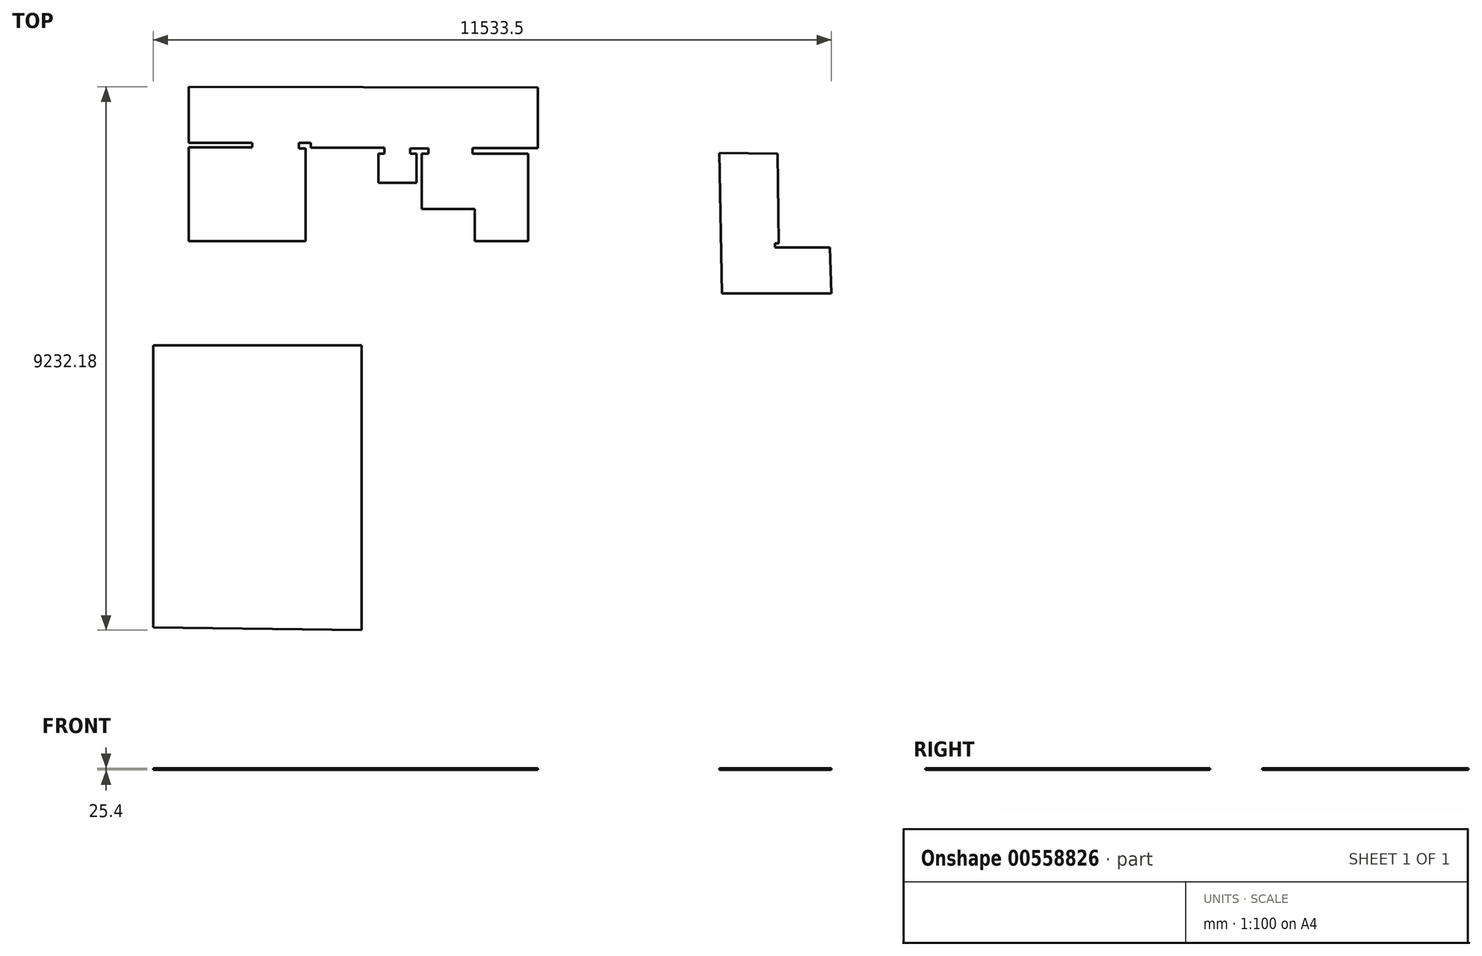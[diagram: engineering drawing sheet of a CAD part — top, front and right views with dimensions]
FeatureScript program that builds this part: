
annotation { "Feature Type Name" : "Feature", "Feature Type Description" : "" }
export const myFeature = defineFeature(function(context is Context, id is Id, definition is map)
    precondition{}
    {
        {
            var Q0;
            Q0=qCreatedBy(makeId("Top.planeOp"),FACE);
            var sketch = newSketch(context, id + "F0", { "sketchPlane" : qUnion([Q0])});
            skLineSegment(sketch, "E0", {"start": v(-2726.1, -5017.5) * mm, "end": v(4588.5, -5111.42) * mm});
            skLineSegment(sketch, "E1", {"start": v(4588.5, -5111.42) * mm, "end": v(4518.76, -1894.4) * mm});
            skLineSegment(sketch, "E2", {"start": v(4518.76, -1894.4) * mm, "end": v(3916.86, -1894.4) * mm});
            skLineSegment(sketch, "E3", {"start": v(3916.86, -1894.4) * mm, "end": v(3916.86, 807.93) * mm});
            skLineSegment(sketch, "E4", {"start": v(3916.86, 807.93) * mm, "end": v(3335.71, 807.93) * mm});
            skLineSegment(sketch, "E5", {"start": v(3335.71, 807.93) * mm, "end": v(3335.71, 1418.13) * mm});
            skLineSegment(sketch, "E6", {"start": v(3335.71, 1418.13) * mm, "end": v(2580.22, 1418.13) * mm});
            skLineSegment(sketch, "E7", {"start": v(2580.22, 1418.13) * mm, "end": v(2580.22, 807.93) * mm});
            skLineSegment(sketch, "E8", {"start": v(2580.22, 807.93) * mm, "end": v(2007.38, 807.93) * mm});
            skLineSegment(sketch, "E9", {"start": v(2007.38, 807.93) * mm, "end": v(2007.38, 1418.13) * mm});
            skLineSegment(sketch, "E10", {"start": v(2007.38, 1418.13) * mm, "end": v(1114.9, 1418.13) * mm});
            skLineSegment(sketch, "E11", {"start": v(1114.9, 1418.13) * mm, "end": v(1114.9, 712.46) * mm});
            skLineSegment(sketch, "E12", {"start": v(1114.9, 712.46) * mm, "end": v(1027.73, 716.6) * mm});
            skLineSegment(sketch, "E13", {"start": v(1027.73, 716.6) * mm, "end": v(1027.73, 1675.5) * mm});
            skLineSegment(sketch, "E14", {"start": v(1027.73, 1675.5) * mm, "end": v(1106.6, 1675.5) * mm});
            skLineSegment(sketch, "E15", {"start": v(1106.6, 1675.5) * mm, "end": v(1106.6, 1501.15) * mm});
            skLineSegment(sketch, "E16", {"start": v(1106.6, 1501.15) * mm, "end": v(1758.32, 1501.15) * mm});
            skLineSegment(sketch, "E17", {"start": v(1758.32, 1501.15) * mm, "end": v(1758.32, 2443.44) * mm});
            skLineSegment(sketch, "E18", {"start": v(1758.32, 2443.44) * mm, "end": v(1114.9, 2443.44) * mm});
            skLineSegment(sketch, "E19", {"start": v(1114.9, 2443.44) * mm, "end": v(1114.9, 2273.25) * mm});
            skLineSegment(sketch, "E20", {"start": v(1114.9, 2273.25) * mm, "end": v(1027.73, 2273.25) * mm});
            skLineSegment(sketch, "E21", {"start": v(1027.73, 2273.25) * mm, "end": v(1027.73, 3124.21) * mm});
            skLineSegment(sketch, "E22", {"start": v(1027.73, 3124.21) * mm, "end": v(-43.24, 3124.21) * mm});
            skLineSegment(sketch, "E23", {"start": v(-43.24, 3124.21) * mm, "end": v(-43.24, 733.21) * mm});
            skLineSegment(sketch, "E24", {"start": v(-43.24, 733.21) * mm, "end": v(-300.6, 733.21) * mm});
            skLineSegment(sketch, "E25", {"start": v(-300.6, 733.21) * mm, "end": v(-300.6, 832.84) * mm});
            skLineSegment(sketch, "E26", {"start": v(-300.6, 832.84) * mm, "end": v(-130.4, 832.84) * mm});
            skLineSegment(sketch, "E27", {"start": v(-130.4, 832.84) * mm, "end": v(-130.4, 1418.13) * mm});
            skLineSegment(sketch, "E28", {"start": v(-130.4, 1418.13) * mm, "end": v(-1209.68, 1418.13) * mm});
            skLineSegment(sketch, "E29", {"start": v(-1209.68, 1418.13) * mm, "end": v(-1209.68, 832.84) * mm});
            skLineSegment(sketch, "E30", {"start": v(-1209.68, 832.84) * mm, "end": v(-1051.94, 832.84) * mm});
            skLineSegment(sketch, "E31", {"start": v(-1051.94, 832.84) * mm, "end": v(-1051.94, 733.21) * mm});
            skLineSegment(sketch, "E32", {"start": v(-1051.94, 733.21) * mm, "end": v(-1317.6, 733.21) * mm});
            skLineSegment(sketch, "E33", {"start": v(-1317.6, 733.21) * mm, "end": v(-1317.6, 1418.13) * mm});
            skLineSegment(sketch, "E34", {"start": v(-1317.6, 1418.13) * mm, "end": v(-2728.96, 1418.13) * mm});
            skLineSegment(sketch, "E35", {"start": v(-2728.96, 1418.13) * mm, "end": v(-2726.1, -5017.5) * mm});
            skLineSegment(sketch, "E36", {"start": v(6899.05, 3048.2) * mm, "end": v(6945.42, 662.88) * mm});
            skLineSegment(sketch, "E37", {"start": v(6945.42, 662.88) * mm, "end": v(8805.24, 662.88) * mm});
            skLineSegment(sketch, "E38", {"start": v(8805.24, 662.88) * mm, "end": v(8782.06, 1443.4) * mm});
            skLineSegment(sketch, "E39", {"start": v(8782.06, 1443.4) * mm, "end": v(7844.42, 1443.4) * mm});
            skLineSegment(sketch, "E40", {"start": v(7844.42, 1443.4) * mm, "end": v(7844.42, 1511.5) * mm});
            skLineSegment(sketch, "E41", {"start": v(7844.42, 1511.5) * mm, "end": v(7911.9, 1511.5) * mm});
            skLineSegment(sketch, "E42", {"start": v(7911.9, 1511.5) * mm, "end": v(7888.2, 3035.32) * mm});
            skLineSegment(sketch, "E43", {"start": v(7888.2, 3035.32) * mm, "end": v(6899.05, 3048.2) * mm});
            skLineSegment(sketch, "E44", {"start": v(-2124.29, 4169.2) * mm, "end": v(-2124.29, 3216.23) * mm});
            skLineSegment(sketch, "E45", {"start": v(-47.83, 3216.23) * mm, "end": v(-47.83, 3138.55) * mm});
            skLineSegment(sketch, "E46", {"start": v(-47.83, 3138.55) * mm, "end": v(1207, 3138.55) * mm});
            skLineSegment(sketch, "E47", {"start": v(1207, 3138.55) * mm, "end": v(1207, 3036.06) * mm});
            skLineSegment(sketch, "E48", {"start": v(1207, 3036.06) * mm, "end": v(1105.9, 3036.06) * mm});
            skLineSegment(sketch, "E49", {"start": v(1105.9, 3036.06) * mm, "end": v(1105.9, 2538.17) * mm});
            skLineSegment(sketch, "E50", {"start": v(1105.9, 2538.17) * mm, "end": v(1749.31, 2538.17) * mm});
            skLineSegment(sketch, "E51", {"start": v(1749.31, 2538.17) * mm, "end": v(1749.31, 3036.06) * mm});
            skLineSegment(sketch, "E52", {"start": v(1749.31, 3036.06) * mm, "end": v(1646.28, 3036.06) * mm});
            skLineSegment(sketch, "E53", {"start": v(1646.28, 3036.06) * mm, "end": v(1646.28, 3125.48) * mm});
            skLineSegment(sketch, "E54", {"start": v(1646.28, 3125.48) * mm, "end": v(1952.81, 3125.48) * mm});
            skLineSegment(sketch, "E55", {"start": v(1952.81, 3125.48) * mm, "end": v(1952.81, 3036.06) * mm});
            skLineSegment(sketch, "E56", {"start": v(1952.81, 3036.06) * mm, "end": v(1839.47, 3036.06) * mm});
            skLineSegment(sketch, "E57", {"start": v(1839.47, 3036.06) * mm, "end": v(1839.47, 2095.1) * mm});
            skLineSegment(sketch, "E58", {"start": v(1839.47, 2095.1) * mm, "end": v(2738.47, 2095.1) * mm});
            skLineSegment(sketch, "E59", {"start": v(2738.47, 2095.1) * mm, "end": v(2738.47, 1549.01) * mm});
            skLineSegment(sketch, "E60", {"start": v(2738.47, 1549.01) * mm, "end": v(3647.77, 1549.01) * mm});
            skLineSegment(sketch, "E61", {"start": v(3647.77, 1549.01) * mm, "end": v(3647.77, 3036.06) * mm});
            skLineSegment(sketch, "E62", {"start": v(3647.77, 3036.06) * mm, "end": v(2702.4, 3036.06) * mm});
            skLineSegment(sketch, "E63", {"start": v(2702.4, 3036.06) * mm, "end": v(2702.4, 3128.06) * mm});
            skLineSegment(sketch, "E64", {"start": v(2702.4, 3128.06) * mm, "end": v(3815.2, 3128.06) * mm});
            skLineSegment(sketch, "E65", {"start": v(3815.2, 3128.06) * mm, "end": v(3815.2, 4158.43) * mm});
            skLineSegment(sketch, "E66", {"start": v(3815.2, 4158.43) * mm, "end": v(-2124.29, 4169.2) * mm});
            skLineSegment(sketch, "E67", {"start": v(-2124.29, 3216.23) * mm, "end": v(-1044.78, 3216.23) * mm});
            skLineSegment(sketch, "E68", {"start": v(-1044.78, 3216.23) * mm, "end": v(-1044.78, 3141.63) * mm});
            skLineSegment(sketch, "E69", {"start": v(-1044.78, 3141.63) * mm, "end": v(-2124.29, 3141.63) * mm});
            skLineSegment(sketch, "E70", {"start": v(-2124.29, 3141.63) * mm, "end": v(-2124.29, 1552.13) * mm});
            skLineSegment(sketch, "E71", {"start": v(-2124.29, 1552.13) * mm, "end": v(-134.37, 1552.13) * mm});
            skLineSegment(sketch, "E72", {"start": v(-134.37, 1552.13) * mm, "end": v(-134.37, 3127.1) * mm});
            skLineSegment(sketch, "E73", {"start": v(-134.37, 3127.1) * mm, "end": v(-250.02, 3127.1) * mm});
            skLineSegment(sketch, "E74", {"start": v(-250.02, 3127.1) * mm, "end": v(-250.02, 3216.23) * mm});
            skLineSegment(sketch, "E75", {"start": v(-250.02, 3216.23) * mm, "end": v(-47.83, 3216.23) * mm});
            skLineSegment(sketch, "E76", {"start": v(1101.98, -290.4) * mm, "end": v(1101.98, -1875.22) * mm});
            skLineSegment(sketch, "E77", {"start": v(1101.98, -1875.22) * mm, "end": v(3063.36, -1875.22) * mm});
            skLineSegment(sketch, "E78", {"start": v(3063.36, -1875.22) * mm, "end": v(3063.36, -1289.1) * mm});
            skLineSegment(sketch, "E79", {"start": v(3063.36, -1289.1) * mm, "end": v(1720.84, -1289.1) * mm});
            skLineSegment(sketch, "E80", {"start": v(1720.84, -1289.1) * mm, "end": v(1720.84, -290.4) * mm});
            skLineSegment(sketch, "E81", {"start": v(1720.84, -290.4) * mm, "end": v(1101.98, -290.4) * mm});
            skLineSegment(sketch, "E82.bottom", {"start": v(-2728.23, -222.23) * mm, "end": v(816.13, -222.23) * mm});
            skLineSegment(sketch, "E82.top", {"start": v(-2728.23, -5062.98) * mm, "end": v(816.13, -5062.98) * mm});
            skLineSegment(sketch, "E82.left", {"start": v(-2728.23, -222.23) * mm, "end": v(-2728.23, -5062.98) * mm});
            skLineSegment(sketch, "E82.right", {"start": v(816.13, -222.23) * mm, "end": v(816.13, -5062.98) * mm});
            skSolve(sketch);
        }
        {
            var Q0;
            Q0=makeQuery(id+"F0.imprint","IMPRINT",FACE,{"disambiguationData":[TD([[makeQuery(id+"F0.imprint","IMPRINT",EDGE,{"derivedFrom":sQuery(id+"F0.wireOp",EDGE,"E0")}),1.0]])]});
            extrude(context, id + "F1", {"entities" : qUnion([Q0]), "depth" : 25.4 * mm, "offsetDistance" : 25.4 * mm});
        }
        {
            var Q0;
            Q0=makeQuery(id+"F0.imprint","IMPRINT",FACE,{"disambiguationData":[TD([[makeQuery(id+"F0.imprint","IMPRINT",EDGE,{"derivedFrom":sQuery(id+"F0.wireOp",EDGE,"E36")}),1.0]])]});
            extrude(context, id + "F2", {"entities" : qUnion([Q0]), "depth" : 25.4 * mm, "offsetDistance" : 25.4 * mm});
        }
        {
            var Q0;
            Q0=makeQuery(id+"F0.imprint","IMPRINT",FACE,{"disambiguationData":[TD([[makeQuery(id+"F0.imprint","IMPRINT",EDGE,{"derivedFrom":sQuery(id+"F0.wireOp",EDGE,"E44")}),1.0]])]});
            extrude(context, id + "F3", {"entities" : qUnion([Q0]), "depth" : 25.4 * mm, "offsetDistance" : 25.4 * mm});
        }
    });
